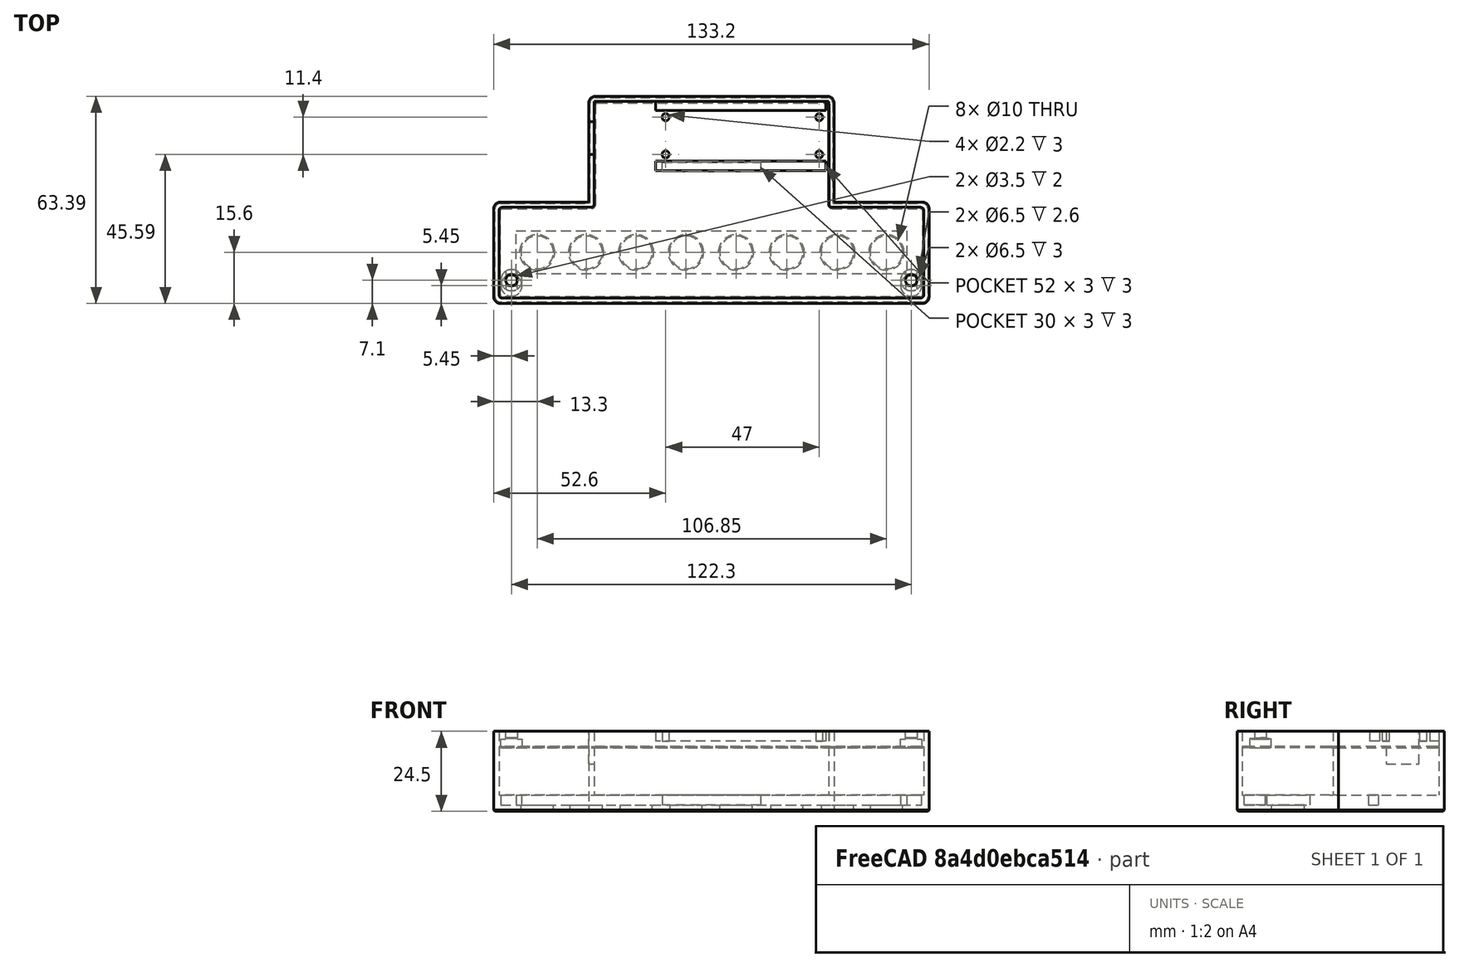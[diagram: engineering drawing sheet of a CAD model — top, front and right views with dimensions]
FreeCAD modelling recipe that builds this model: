
FCSTD DOCUMENT  (FreeCAD 0.21R33771 (Git))
Label: Makerverse_Keyboard_Case_V1
License: All rights reserved
LicenseURL: https://en.wikipedia.org/wiki/All_rights_reserved
objects: TechDraw::DrawViewDimension×38, Sketcher::SketchObject×12, PartDesign::Pocket×10, TechDraw::DrawViewPart×4, PartDesign::Pad×2, PartDesign::Chamfer×2, PartDesign::Body×2, TechDraw::DrawSVGTemplate×1, TechDraw::DrawPage×1
note: 106 computed .brp shape members not serialized (recipe doc carries the construction recipe); baked Part::Feature solids carry a one-line shape summary decoded from their .brp

FEATURE [Sketcher::SketchObject] Sketch
  FullyConstrained = true
  MapMode = 5
  Support = -> [XY_Plane]
  sketch-geometry (20):
    g0: LineSegment StartX=2 StartY=0 StartZ=0 EndX=131.2 EndY=0 EndZ=0
    g1: LineSegment StartX=133.2 StartY=2 StartZ=0 EndX=133.2 EndY=29 EndZ=0
    g2: LineSegment StartX=131.2 StartY=31 StartZ=0 EndX=104.1 EndY=31 EndZ=0
    g3: LineSegment StartX=104.1 StartY=31 StartZ=0 EndX=104.1 EndY=61.39 EndZ=0
    g4: LineSegment StartX=102.1 StartY=63.39 StartZ=0 EndX=31.1 EndY=63.39 EndZ=0
    g5: LineSegment StartX=29.1 StartY=61.39 StartZ=0 EndX=29.1 EndY=31 EndZ=0
    g6: LineSegment StartX=29.1 StartY=31 StartZ=0 EndX=2 EndY=31 EndZ=0
    g7: LineSegment StartX=0 StartY=29 StartZ=0 EndX=0 EndY=2 EndZ=0
    g8: ArcOfCircle CenterX=31.1 CenterY=61.39 CenterZ=0 NormalX=0 NormalY=0 NormalZ=1 AngleXU=0 Radius=2 StartAngle=1.5708 EndAngle=3.14159
    g9: GeomPoint X=29.1 Y=63.39 Z=0
    g10: ArcOfCircle CenterX=102.1 CenterY=61.39 CenterZ=0 NormalX=0 NormalY=0 NormalZ=1 AngleXU=0 Radius=2 StartAngle=-1.8e-15 EndAngle=1.5708
    g11: GeomPoint X=104.1 Y=63.39 Z=0
    g12: ArcOfCircle CenterX=131.2 CenterY=29 CenterZ=0 NormalX=0 NormalY=0 NormalZ=1 AngleXU=0 Radius=2 StartAngle=0 EndAngle=1.5708
    g13: GeomPoint X=133.2 Y=31 Z=0
    g14: ArcOfCircle CenterX=131.2 CenterY=2 CenterZ=0 NormalX=0 NormalY=0 NormalZ=1 AngleXU=0 Radius=2 StartAngle=4.71239 EndAngle=6.28319
    g15: GeomPoint X=133.2 Y=0 Z=0
    g16: ArcOfCircle CenterX=2 CenterY=2 CenterZ=0 NormalX=0 NormalY=0 NormalZ=1 AngleXU=0 Radius=2 StartAngle=3.14159 EndAngle=4.71239
    g17: GeomPoint X=0 Y=0 Z=0
    g18: ArcOfCircle CenterX=2 CenterY=29 CenterZ=0 NormalX=0 NormalY=0 NormalZ=1 AngleXU=0 Radius=2 StartAngle=1.5708 EndAngle=3.14159
    g19: GeomPoint X=0 Y=31 Z=0
  constraints (47):
    c: Coincident(g-1,g17)
    c: PointOnObject(g15,g-1)
    c: Vertical(g1)
    c: Horizontal(g2)
    c: Coincident(g2,g3)
    c: Vertical(g3)
    c: Horizontal(g4)
    c: Vertical(g5)
    c: Coincident(g5,g6)
    c: PointOnObject(g19,g-2)
    c: Horizontal(g6)
    c: DistanceX(g17,g15) = 133.2
    c: DistanceX(g19,g6) = 29.1
    c: DistanceX(g2,g13) = 29.1
    c: DistanceY(g17,g19) = 31
    c: DistanceY(g2,g5) = 0
    c: PointOnObject(g9,g5)
    c: PointOnObject(g9,g4)
    c: Tangent(g5,g8) = -1.5708
    c: Tangent(g4,g8) = -1.5708
    c: DistanceX(g5,g8) = 2
    c: PointOnObject(g11,g3)
    c: PointOnObject(g11,g4)
    c: Tangent(g3,g10) = -1.5708
    c: Tangent(g4,g10) = -1.5708
    c: PointOnObject(g13,g2)
    c: PointOnObject(g13,g1)
    c: Tangent(g2,g12) = -1.5708
    c: Tangent(g1,g12) = -1.5708
    c: PointOnObject(g15,g0)
    c: PointOnObject(g15,g1)
    c: Tangent(g0,g14) = -1.5708
    c: Tangent(g1,g14) = -1.5708
    c: PointOnObject(g17,g0)
    c: PointOnObject(g17,g7)
    c: Tangent(g0,g16) = -1.5708
    c: Tangent(g7,g16) = -1.5708
    c: PointOnObject(g19,g7)
    c: PointOnObject(g19,g6)
    c: Tangent(g7,g18) = -1.5708
    c: Tangent(g6,g18) = -1.5708
    c: DistanceX(g7,g18) = 2
    c: DistanceX(g7,g16) = 2
    c: DistanceX(g12,g1) = 2
    c: DistanceX(g10,g3) = 2
    c: DistanceY(g0,g14) = 2
    c: DistanceY(g5,g8) = 30.39
FEATURE [PartDesign::Pad] Pad
  Direction = (0,0,1)
  Length = 24.5
  Length2 = 10
  Profile = -> Sketch
  ReferenceAxis = -> Sketch [N_Axis]
  Type = 0
FEATURE [Sketcher::SketchObject] Sketch001
  ExternalGeometry = -> [Pad]
  FullyConstrained = true
  MapMode = 5
  Placement = pos=(0,0,0) rot=(1,0,0;3.14159rad)
  Support = -> [Pad]
  sketch-geometry (20):
    g0: LineSegment StartX=2.6 StartY=-1.6 StartZ=0 EndX=130.6 EndY=-1.6 EndZ=0
    g1: LineSegment StartX=131.6 StartY=-2.6 StartZ=0 EndX=131.6 EndY=-28.4 EndZ=0
    g2: LineSegment StartX=130.6 StartY=-29.4 StartZ=0 EndX=103.5 EndY=-29.4 EndZ=0
    g3: LineSegment StartX=102.5 StartY=-30.4 StartZ=0 EndX=102.5 EndY=-61.79 EndZ=0
    g4: LineSegment StartX=102.5 StartY=-61.79 StartZ=0 EndX=30.7 EndY=-61.79 EndZ=0
    g5: LineSegment StartX=30.7 StartY=-61.79 StartZ=0 EndX=30.7 EndY=-30.4 EndZ=0
    g6: LineSegment StartX=29.7 StartY=-29.4 StartZ=0 EndX=2.6 EndY=-29.4 EndZ=0
    g7: LineSegment StartX=1.6 StartY=-28.4 StartZ=0 EndX=1.6 EndY=-2.6 EndZ=0
    g8: ArcOfCircle CenterX=2.6 CenterY=-2.6 CenterZ=0 NormalX=0 NormalY=0 NormalZ=1 AngleXU=0 Radius=1 StartAngle=1.5708 EndAngle=3.14159
    g9: GeomPoint X=1.6 Y=-1.6 Z=0
    g10: ArcOfCircle CenterX=2.6 CenterY=-28.4 CenterZ=0 NormalX=0 NormalY=0 NormalZ=1 AngleXU=0 Radius=1 StartAngle=3.14159 EndAngle=4.71239
    g11: GeomPoint X=1.6 Y=-29.4 Z=0
    g12: ArcOfCircle CenterX=29.7 CenterY=-30.4 CenterZ=0 NormalX=0 NormalY=0 NormalZ=1 AngleXU=0 Radius=1 StartAngle=0 EndAngle=1.5708
    g13: GeomPoint X=30.7 Y=-29.4 Z=0
    g14: ArcOfCircle CenterX=103.5 CenterY=-30.4 CenterZ=0 NormalX=0 NormalY=0 NormalZ=1 AngleXU=0 Radius=1 StartAngle=1.5708 EndAngle=3.14159
    g15: GeomPoint X=102.5 Y=-29.4 Z=0
    g16: ArcOfCircle CenterX=130.6 CenterY=-28.4 CenterZ=0 NormalX=0 NormalY=0 NormalZ=1 AngleXU=0 Radius=1 StartAngle=4.71239 EndAngle=6.28319
    g17: GeomPoint X=131.6 Y=-29.4 Z=0
    g18: ArcOfCircle CenterX=130.6 CenterY=-2.6 CenterZ=0 NormalX=0 NormalY=0 NormalZ=1 AngleXU=0 Radius=1 StartAngle=0 EndAngle=1.5708
    g19: GeomPoint X=131.6 Y=-1.6 Z=0
  constraints (49):
    c: Horizontal(g0)
    c: Vertical(g1)
    c: Horizontal(g2)
    c: Vertical(g3)
    c: Coincident(g3,g4)
    c: Horizontal(g4)
    c: Coincident(g4,g5)
    c: Vertical(g5)
    c: Horizontal(g6)
    c: Parallel(g7,g-2)
    c: DistanceX(g9,g19) = 130
    c: DistanceX(g-1,g-3) = 133.2
    c: DistanceX(g-1,g9) = 1.6
    c: DistanceY(g9,g-1) = 1.6
    c: DistanceY(g-4,g11) = 1.6
    c: DistanceX(g-4,g13) = 1.6
    c: DistanceY(g-6,g17) = 1.6
    c: DistanceX(g15,g-6) = 1.6
    c: DistanceY(g-5,g3) = 1.6
    c: PointOnObject(g9,g7)
    c: PointOnObject(g9,g0)
    c: Tangent(g7,g8) = 1.5708
    c: Tangent(g0,g8) = 1.5708
    c: DistanceX(g7,g8) = 1
    c: PointOnObject(g11,g6)
    c: PointOnObject(g11,g7)
    c: Tangent(g6,g10) = 1.5708
    c: Tangent(g7,g10) = 1.5708
    c: PointOnObject(g13,g5)
    c: PointOnObject(g13,g6)
    c: Tangent(g5,g12) = -1.5708
    c: Tangent(g6,g12) = -1.5708
    c: PointOnObject(g15,g3)
    c: PointOnObject(g15,g2)
    c: Tangent(g3,g14) = -1.5708
    c: Tangent(g2,g14) = -1.5708
    c: PointOnObject(g17,g2)
    c: PointOnObject(g17,g1)
    c: Tangent(g2,g16) = 1.5708
    c: Tangent(g1,g16) = 1.5708
    c: PointOnObject(g19,g1)
    c: PointOnObject(g19,g0)
    c: Tangent(g1,g18) = 1.5708
    c: Tangent(g0,g18) = 1.5708
    c: DistanceX(g18,g1) = 1
    c: DistanceX(g16,g1) = 1
    c: DistanceY(g14,g2) = 1
    c: DistanceX(g12,g5) = 1
    c: DistanceY(g6,g10) = 1
FEATURE [PartDesign::Pocket] Pocket
  BaseFeature = -> Pad
  Direction = (0,0,1)
  Length = 19.5
  Length2 = 5
  Profile = -> Sketch001
  ReferenceAxis = -> Sketch001 [N_Axis]
  Type = 0
FEATURE [Sketcher::SketchObject] Sketch002
  ExternalGeometry = -> [Pocket]
  FullyConstrained = true
  MapMode = 5
  Placement = pos=(0,0,19.5) rot=(1,0,0;3.14159rad)
  Support = -> [Pocket]
  sketch-geometry (4):
    g0: LineSegment StartX=126.4 StartY=-22.2 StartZ=0 EndX=6.8 EndY=-22.2 EndZ=0
    g1: LineSegment StartX=6.8 StartY=-22.2 StartZ=0 EndX=6.8 EndY=-9 EndZ=0
    g2: LineSegment StartX=6.8 StartY=-9 StartZ=0 EndX=126.4 EndY=-9 EndZ=0
    g3: LineSegment StartX=126.4 StartY=-9 StartZ=0 EndX=126.4 EndY=-22.2 EndZ=0
  constraints (12):
    c: Coincident(g0,g1)
    c: Coincident(g1,g2)
    c: Coincident(g2,g3)
    c: Coincident(g3,g0)
    c: Horizontal(g0)
    c: Horizontal(g2)
    c: Vertical(g1)
    c: Vertical(g3)
    c: DistanceY(g3,g3) = 13.2
    c: DistanceX(g0,g-3) = 5.2
    c: DistanceX(g-4,g0) = 5.2
    c: DistanceY(g2,g-5) = 7.4
FEATURE [PartDesign::Pocket] Pocket001
  BaseFeature = -> Pocket
  Direction = (0,0,1)
  Length = 3
  Length2 = 5
  Profile = -> Sketch002
  ReferenceAxis = -> Sketch002 [N_Axis]
  Type = 0
FEATURE [Sketcher::SketchObject] Sketch003
  ExternalGeometry = -> [Pocket001]
  FullyConstrained = true
  MapMode = 5
  Placement = pos=(0,0,22.5) rot=(1,0,0;3.14159rad)
  Support = -> [Pocket001]
  sketch-geometry (9):
    g0: Circle CenterX=59.05 CenterY=-15.6 CenterZ=0 NormalX=0 NormalY=0 NormalZ=1 AngleXU=0 Radius=5
    g1: Circle CenterX=43.55 CenterY=-15.6 CenterZ=0 NormalX=0 NormalY=0 NormalZ=1 AngleXU=0 Radius=5
    g2: Circle CenterX=74.4 CenterY=-15.6 CenterZ=0 NormalX=0 NormalY=0 NormalZ=1 AngleXU=0 Radius=5
    g3: LineSegment StartX=6.8 StartY=-15.6 StartZ=0 EndX=126.4 EndY=-15.6 EndZ=0
    g4: Circle CenterX=28.05 CenterY=-15.6 CenterZ=0 NormalX=0 NormalY=0 NormalZ=1 AngleXU=0 Radius=5
    g5: Circle CenterX=13.05 CenterY=-15.6 CenterZ=0 NormalX=0 NormalY=0 NormalZ=1 AngleXU=0 Radius=5
    g6: Circle CenterX=89.65 CenterY=-15.6 CenterZ=0 NormalX=0 NormalY=0 NormalZ=1 AngleXU=0 Radius=5
    g7: Circle CenterX=104.9 CenterY=-15.6 CenterZ=0 NormalX=0 NormalY=0 NormalZ=1 AngleXU=0 Radius=5
    g8: Circle CenterX=119.9 CenterY=-15.6 CenterZ=0 NormalX=0 NormalY=0 NormalZ=1 AngleXU=0 Radius=5
  constraints (29):
    c: Diameter(g0) = 10
    c: DistanceX(g1,g0) = 15.5
    c: Diameter(g2) = 10
    c: Diameter(g1) = 10
    c: PointOnObject(g3,g-3)
    c: PointOnObject(g3,g-4)
    c: Horizontal(g3)
    c: DistanceY(g3,g-4) = 6.6
    c: PointOnObject(g2,g3)
    c: PointOnObject(g1,g3)
    c: PointOnObject(g0,g3)
    c: PointOnObject(g4,g3)
    c: PointOnObject(g5,g3)
    c: Diameter(g4) = 10
    c: Diameter(g5) = 10
    c: DistanceX(g4,g1) = 15.5
    c: DistanceX(g5,g4) = 15
    c: PointOnObject(g6,g3)
    c: PointOnObject(g7,g3)
    c: PointOnObject(g8,g3)
    c: DistanceX(g7,g8) = 15
    c: Diameter(g6) = 10
    c: Diameter(g7) = 10
    c: Diameter(g8) = 10
    c: DistanceX(g3,g5) = 6.25
    c: DistanceX(g8,g-4) = 6.5
    c: DistanceX(g6,g7) = 15.25
    c: DistanceX(g2,g6) = 15.25
    c: DistanceY(g-4,g-4) = 13.2
FEATURE [PartDesign::Pocket] Pocket002
  BaseFeature = -> Pocket001
  Direction = (0,0,1)
  Length = 5
  Length2 = 5
  Profile = -> Sketch003
  ReferenceAxis = -> Sketch003 [N_Axis]
  Type = 1
FEATURE [Sketcher::SketchObject] Sketch006
  FullyConstrained = true
  MapMode = 5
  Support = -> [XY_Plane001]
  sketch-geometry (24):
    g0: LineSegment StartX=2.6 StartY=29.4 StartZ=0 EndX=29.6 EndY=29.4 EndZ=0
    g1: LineSegment StartX=30.6 StartY=30.4 StartZ=0 EndX=30.6 EndY=60.79 EndZ=0
    g2: LineSegment StartX=31.6 StartY=61.79 StartZ=0 EndX=101.4 EndY=61.79 EndZ=0
    g3: LineSegment StartX=102.4 StartY=60.79 StartZ=0 EndX=102.4 EndY=30.4 EndZ=0
    g4: LineSegment StartX=103.4 StartY=29.4 StartZ=0 EndX=130.6 EndY=29.4 EndZ=0
    g5: LineSegment StartX=131.6 StartY=28.4 StartZ=0 EndX=131.6 EndY=2.6 EndZ=0
    g6: LineSegment StartX=130.6 StartY=1.6 StartZ=0 EndX=2.6 EndY=1.6 EndZ=0
    g7: LineSegment StartX=1.6 StartY=28.4 StartZ=0 EndX=1.6 EndY=2.6 EndZ=0
    g8: ArcOfCircle CenterX=2.6 CenterY=2.6 CenterZ=0 NormalX=0 NormalY=0 NormalZ=1 AngleXU=0 Radius=1 StartAngle=3.14159 EndAngle=4.71239
    g9: GeomPoint X=1.6 Y=1.6 Z=0
    g10: ArcOfCircle CenterX=130.6 CenterY=2.6 CenterZ=0 NormalX=0 NormalY=0 NormalZ=1 AngleXU=0 Radius=1 StartAngle=4.71239 EndAngle=6.28319
    g11: GeomPoint X=131.6 Y=1.6 Z=0
    g12: ArcOfCircle CenterX=130.6 CenterY=28.4 CenterZ=0 NormalX=0 NormalY=0 NormalZ=1 AngleXU=0 Radius=1 StartAngle=1.1e-15 EndAngle=1.5708
    g13: GeomPoint X=131.6 Y=29.4 Z=0
    g14: ArcOfCircle CenterX=2.6 CenterY=28.4 CenterZ=0 NormalX=0 NormalY=0 NormalZ=1 AngleXU=0 Radius=1 StartAngle=1.5708 EndAngle=3.14159
    g15: GeomPoint X=1.6 Y=29.4 Z=0
    g16: ArcOfCircle CenterX=31.6 CenterY=60.79 CenterZ=0 NormalX=0 NormalY=0 NormalZ=1 AngleXU=0 Radius=1 StartAngle=1.5708 EndAngle=3.14159
    g17: GeomPoint X=30.6 Y=61.79 Z=0
    g18: ArcOfCircle CenterX=29.6 CenterY=30.4 CenterZ=0 NormalX=0 NormalY=0 NormalZ=1 AngleXU=0 Radius=1 StartAngle=4.71239 EndAngle=6.28319
    g19: GeomPoint X=30.6 Y=29.4 Z=0
    g20: ArcOfCircle CenterX=103.4 CenterY=30.4 CenterZ=0 NormalX=0 NormalY=0 NormalZ=1 AngleXU=0 Radius=1 StartAngle=3.14159 EndAngle=4.71239
    g21: GeomPoint X=102.4 Y=29.4 Z=0
    g22: ArcOfCircle CenterX=101.4 CenterY=60.79 CenterZ=0 NormalX=0 NormalY=0 NormalZ=1 AngleXU=0 Radius=1 StartAngle=-1.8e-15 EndAngle=1.5708
    g23: GeomPoint X=102.4 Y=61.79 Z=0
  constraints (56):
    c: Horizontal(g0)
    c: Vertical(g1)
    c: Horizontal(g2)
    c: Vertical(g3)
    c: Horizontal(g4)
    c: Vertical(g5)
    c: Horizontal(g6)
    c: Vertical(g7)
    c: DistanceX(g9,g11) = 130
    c: DistanceY(g11,g13) = 27.8
    c: DistanceY(g19,g21) = 0
    c: DistanceX(g21,g13) = 29.2
    c: DistanceX(g17,g23) = 71.8
    c: DistanceY(g21,g23) = 32.39
    c: DistanceX(g-1,g9) = 1.6
    c: DistanceY(g-1,g9) = 1.6
    c: PointOnObject(g9,g6)
    c: PointOnObject(g9,g7)
    c: Tangent(g6,g8) = 1.5708
    c: Tangent(g7,g8) = -1.5708
    c: PointOnObject(g11,g6)
    c: PointOnObject(g11,g5)
    c: Tangent(g6,g10) = 1.5708
    c: Tangent(g5,g10) = 1.5708
    c: PointOnObject(g13,g5)
    c: PointOnObject(g13,g4)
    c: Tangent(g5,g12) = 1.5708
    c: Tangent(g4,g12) = 1.5708
    c: PointOnObject(g15,g7)
    c: PointOnObject(g15,g0)
    c: Tangent(g7,g14) = -1.5708
    c: Tangent(g0,g14) = 1.5708
    c: DistanceX(g7,g14) = 1
    c: DistanceX(g7,g8) = 1
    c: DistanceX(g10,g5) = 1
    c: DistanceX(g12,g5) = 1
    c: PointOnObject(g17,g1)
    c: PointOnObject(g17,g2)
    c: Tangent(g1,g16) = 1.5708
    c: Tangent(g2,g16) = 1.5708
    c: PointOnObject(g19,g0)
    c: PointOnObject(g19,g1)
    c: Tangent(g0,g18) = -1.5708
    c: Tangent(g1,g18) = -1.5708
    c: PointOnObject(g21,g4)
    c: PointOnObject(g21,g3)
    c: Tangent(g4,g20) = -1.5708
    c: Tangent(g3,g20) = -1.5708
    c: PointOnObject(g23,g3)
    c: PointOnObject(g23,g2)
    c: Tangent(g3,g22) = 1.5708
    c: Tangent(g2,g22) = 1.5708
    c: DistanceX(g1,g16) = 1
    c: DistanceX(g18,g1) = 1
    c: DistanceX(g3,g20) = 1
    c: DistanceX(g22,g3) = 1
FEATURE [PartDesign::Pad] Pad001
  Direction = (0,0,1)
  Length = 5
  Length2 = 10
  Profile = -> Sketch006
  ReferenceAxis = -> Sketch006 [N_Axis]
  Type = 0
FEATURE [Sketcher::SketchObject] Sketch007
  ExternalGeometry = -> [Pocket002]
  FullyConstrained = true
  MapMode = 5
  Placement = pos=(0,0,19.5) rot=(1,0,0;3.14159rad)
  Support = -> [Pocket002]
  sketch-geometry (6):
    g0: LineSegment StartX=51.6 StartY=-40.2 StartZ=0 EndX=81.6 EndY=-40.2 EndZ=0
    g1: LineSegment StartX=81.6 StartY=-40.2 StartZ=0 EndX=81.6 EndY=-43.2 EndZ=0
    g2: LineSegment StartX=81.6 StartY=-43.2 StartZ=0 EndX=51.6 EndY=-43.2 EndZ=0
    g3: LineSegment StartX=51.6 StartY=-43.2 StartZ=0 EndX=51.6 EndY=-40.2 EndZ=0
    g4: Circle CenterX=5.45 CenterY=-5.45 CenterZ=0 NormalX=0 NormalY=0 NormalZ=1 AngleXU=0 Radius=3.25
    g5: Circle CenterX=127.75 CenterY=-5.45 CenterZ=0 NormalX=0 NormalY=0 NormalZ=1 AngleXU=0 Radius=3.25
  constraints (19):
    c: Coincident(g0,g1)
    c: Coincident(g1,g2)
    c: Coincident(g2,g3)
    c: Coincident(g3,g0)
    c: Horizontal(g0)
    c: Horizontal(g2)
    c: Vertical(g1)
    c: Vertical(g3)
    c: DistanceY(g3,g3) = 3
    c: DistanceX(g0,g0) = 30
    c: Diameter(g4) = 6.5
    c: Diameter(g5) = 6.5
    c: DistanceY(g4,g-4) = 3.85
    c: DistanceX(g-3,g4) = 3.85
    c: DistanceY(g5,g-4) = 3.85
    c: DistanceX(g5,g-4) = 2.85
    c: DistanceY(g0,g-5) = 18
    c: DistanceX(g-6,g-7) = 71.8
    c: DistanceX(g0,g-7) = 20.9
FEATURE [PartDesign::Pocket] Pocket003
  BaseFeature = -> Pocket002
  Direction = (0,0,1)
  Length = 3
  Length2 = 5
  Profile = -> Sketch007
  ReferenceAxis = -> Sketch007 [N_Axis]
  Type = 0
FEATURE [Sketcher::SketchObject] Sketch008
  ExternalGeometry = -> [Pocket003]
  FullyConstrained = true
  MapMode = 5
  Placement = pos=(104.1,0,0) rot=(0.57735,0.57735,0.57735;2.0944rad)
  Support = -> [Pocket003]
  sketch-geometry (4):
    g0: LineSegment StartX=45.59 StartY=10 StartZ=0 EndX=55.59 EndY=10 EndZ=0
    g1: LineSegment StartX=55.59 StartY=10 StartZ=0 EndX=55.59 EndY=0 EndZ=0
    g2: LineSegment StartX=55.59 StartY=0 StartZ=0 EndX=45.59 EndY=0 EndZ=0
    g3: LineSegment StartX=45.59 StartY=0 StartZ=0 EndX=45.59 EndY=10 EndZ=0
  constraints (12):
    c: Coincident(g0,g1)
    c: Coincident(g1,g2)
    c: Coincident(g2,g3)
    c: Coincident(g3,g0)
    c: Horizontal(g0)
    c: Horizontal(g2)
    c: Vertical(g1)
    c: Vertical(g3)
    c: PointOnObject(g1,g-1)
    c: DistanceX(g2,g2) = 10
    c: DistanceX(g-4,g0) = 5.39
    c: DistanceY(g1,g1) = 10
FEATURE [PartDesign::Pocket] Pocket004
  BaseFeature = -> Pocket003
  Direction = (-1,0,0)
  Length = 5
  Length2 = 5
  Profile = -> Sketch008
  ReferenceAxis = -> Sketch008 [N_Axis]
  Type = 0
FEATURE [Sketcher::SketchObject] Sketch009
  ExternalGeometry = -> [Pad001]
  FullyConstrained = true
  MapMode = 5
  Placement = pos=(0,0,0) rot=(1,0,0;3.14159rad)
  Support = -> [Pad001]
  sketch-geometry (12):
    g0: Circle CenterX=33.6 CenterY=-45.59 CenterZ=0 NormalX=0 NormalY=0 NormalZ=1 AngleXU=0 Radius=1.1
    g1: Circle CenterX=33.6 CenterY=-56.99 CenterZ=0 NormalX=0 NormalY=0 NormalZ=1 AngleXU=0 Radius=1.1
    g2: Circle CenterX=80.6 CenterY=-45.59 CenterZ=0 NormalX=0 NormalY=0 NormalZ=1 AngleXU=0 Radius=1.1
    g3: Circle CenterX=80.6 CenterY=-56.99 CenterZ=0 NormalX=0 NormalY=0 NormalZ=1 AngleXU=0 Radius=1.1
    g4: LineSegment StartX=31.6 StartY=-58.99 StartZ=0 EndX=83.6 EndY=-58.99 EndZ=0
    g5: LineSegment StartX=83.6 StartY=-58.99 StartZ=0 EndX=83.6 EndY=-61.79 EndZ=0
    g6: LineSegment StartX=83.6 StartY=-61.79 StartZ=0 EndX=31.6 EndY=-61.79 EndZ=0
    g7: LineSegment StartX=31.6 StartY=-61.79 StartZ=0 EndX=31.6 EndY=-58.99 EndZ=0
    g8: LineSegment StartX=31.6 StartY=-40.59 StartZ=0 EndX=83.6 EndY=-40.59 EndZ=0
    g9: LineSegment StartX=83.6 StartY=-40.59 StartZ=0 EndX=83.6 EndY=-43.59 EndZ=0
    g10: LineSegment StartX=83.6 StartY=-43.59 StartZ=0 EndX=31.6 EndY=-43.59 EndZ=0
    g11: LineSegment StartX=31.6 StartY=-43.59 StartZ=0 EndX=31.6 EndY=-40.59 EndZ=0
  constraints (36):
    c: DistanceY(g-4,g1) = 4.8
    c: Diameter(g1) = 2.2
    c: Diameter(g3) = 2.2
    c: Diameter(g2) = 2.2
    c: Diameter(g0) = 2.2
    c: DistanceY(g1,g0) = 11.4
    c: DistanceY(g3,g2) = 11.4
    c: DistanceX(g-3,g1) = 3
    c: DistanceX(g1,g0) = 0
    c: DistanceX(g0,g2) = 47
    c: DistanceX(g3,g2) = 0
    c: DistanceY(g0,g2) = 0
    c: Coincident(g4,g5)
    c: Coincident(g5,g6)
    c: Coincident(g6,g7)
    c: Coincident(g7,g4)
    c: Horizontal(g4)
    c: Horizontal(g6)
    c: Vertical(g5)
    c: Vertical(g7)
    c: Coincident(g8,g9)
    c: Coincident(g9,g10)
    c: Coincident(g10,g11)
    c: Coincident(g11,g8)
    c: Horizontal(g8)
    c: Horizontal(g10)
    c: Vertical(g9)
    c: Vertical(g11)
    c: DistanceX(g10,g10) = 52
    c: DistanceX(g10,g0) = 2
    c: DistanceY(g0,g10) = 2
    c: DistanceY(g11,g11) = 3
    c: DistanceY(g4,g1) = 2
    c: DistanceX(g4,g1) = 2
    c: DistanceX(g4,g4) = 52
    c: DistanceY(g-4,g6) = 0
FEATURE [PartDesign::Pocket] Pocket005
  BaseFeature = -> Pad001
  Direction = (0,0,1)
  Length = 3
  Length2 = 5
  Profile = -> Sketch009
  ReferenceAxis = -> Sketch009 [N_Axis]
  Type = 0
FEATURE [Sketcher::SketchObject] Sketch010
  ExternalGeometry = -> [Pocket005]
  FullyConstrained = true
  MapMode = 5
  Placement = pos=(0,0,5) rot=(0,0,1;0rad)
  Support = -> [Pocket005]
  sketch-geometry (2):
    g0: Circle CenterX=5.45 CenterY=7.1 CenterZ=0 NormalX=0 NormalY=0 NormalZ=1 AngleXU=0 Radius=1.75
    g1: Circle CenterX=127.75 CenterY=7.1 CenterZ=0 NormalX=0 NormalY=0 NormalZ=1 AngleXU=0 Radius=1.75
  constraints (6):
    c: Diameter(g0) = 3.5
    c: Diameter(g1) = 3.5
    c: DistanceX(g-4,g0) = 3.85
    c: DistanceY(g-6,g0) = 5.5
    c: DistanceY(g-6,g1) = 5.5
    c: DistanceX(g1,g-3) = 3.85
FEATURE [PartDesign::Pocket] Pocket006
  BaseFeature = -> Pocket005
  Direction = (0,0,-1)
  Length = 5
  Length2 = 5
  Profile = -> Sketch010
  ReferenceAxis = -> Sketch010 [N_Axis]
  Type = 1
FEATURE [Sketcher::SketchObject] Sketch011
  ExternalGeometry = -> [Pocket006]
  FullyConstrained = true
  MapMode = 5
  Placement = pos=(0,0,5) rot=(0,0,1;0rad)
  Support = -> [Pocket006]
  sketch-geometry (2):
    g0: Circle CenterX=5.45 CenterY=7.1 CenterZ=0 NormalX=0 NormalY=0 NormalZ=1 AngleXU=0 Radius=3.25
    g1: Circle CenterX=127.75 CenterY=7.1 CenterZ=0 NormalX=0 NormalY=0 NormalZ=1 AngleXU=0 Radius=3.25
  constraints (4):
    c: Diameter(g1) = 6.5
    c: Diameter(g0) = 6.5
    c: Coincident(g0,g-4)
    c: Coincident(g-3,g1)
FEATURE [PartDesign::Pocket] Pocket007
  BaseFeature = -> Pocket006
  Direction = (0,0,-1)
  Length = 2.6
  Length2 = 5
  Profile = -> Sketch011
  ReferenceAxis = -> Sketch011 [N_Axis]
  Type = 0
FEATURE [Sketcher::SketchObject] Sketch012
  ExternalGeometry = -> [Pocket007]
  FullyConstrained = true
  MapMode = 5
  Placement = pos=(0,0,2.4) rot=(0,0,1;0rad)
  Support = -> [Pocket007]
  sketch-geometry (8):
    g0: LineSegment StartX=3.7 StartY=4.36139 StartZ=0 EndX=3.7 EndY=9.83861 EndZ=0
    g1: LineSegment StartX=7.2 StartY=9.83861 StartZ=0 EndX=7.2 EndY=4.36139 EndZ=0
    g2: LineSegment StartX=126 StartY=4.36139 StartZ=0 EndX=126 EndY=9.83861 EndZ=0
    g3: LineSegment StartX=129.5 StartY=9.83861 StartZ=0 EndX=129.5 EndY=4.36139 EndZ=0
    g4: ArcOfCircle CenterX=127.75 CenterY=7.1 CenterZ=0 NormalX=0 NormalY=0 NormalZ=1 AngleXU=0 Radius=3.25 StartAngle=4.14378 EndAngle=5.281
    g5: ArcOfCircle CenterX=127.75 CenterY=7.1 CenterZ=0 NormalX=0 NormalY=0 NormalZ=1 AngleXU=0 Radius=3.25 StartAngle=1.00219 EndAngle=2.13941
    g6: ArcOfCircle CenterX=5.45 CenterY=7.1 CenterZ=0 NormalX=0 NormalY=0 NormalZ=1 AngleXU=0 Radius=3.25 StartAngle=1.00219 EndAngle=2.13941
    g7: ArcOfCircle CenterX=5.45 CenterY=7.1 CenterZ=0 NormalX=0 NormalY=0 NormalZ=1 AngleXU=0 Radius=3.25 StartAngle=4.14378 EndAngle=5.281
  constraints (28):
    c: PointOnObject(g0,g-5)
    c: Vertical(g0)
    c: PointOnObject(g1,g-5)
    c: PointOnObject(g1,g-5)
    c: Vertical(g1)
    c: PointOnObject(g2,g-8)
    c: PointOnObject(g2,g-8)
    c: Vertical(g2)
    c: PointOnObject(g3,g-8)
    c: PointOnObject(g3,g-8)
    c: Vertical(g3)
    c: Tangent(g3,g-7)
    c: Tangent(g2,g-7)
    c: Tangent(g0,g-6)
    c: Tangent(g1,g-6)
    c: PointOnObject(g0,g-5)
    c: Coincident(g4,g3)
    c: Coincident(g4,g2)
    c: Tangent(g4,g-8)
    c: Coincident(g5,g2)
    c: Coincident(g5,g3)
    c: Tangent(g5,g-8)
    c: Coincident(g6,g0)
    c: Coincident(g6,g1)
    c: Tangent(g6,g-5)
    c: Coincident(g7,g0)
    c: Coincident(g7,g1)
    c: Tangent(g7,g-5)
FEATURE [PartDesign::Pocket] Pocket008
  BaseFeature = -> Pocket007
  Direction = (0,0,-1)
  Length = 0.2
  Length2 = 5
  Profile = -> Sketch012
  ReferenceAxis = -> Sketch012 [N_Axis]
  Type = 0
FEATURE [Sketcher::SketchObject] Sketch013
  ExternalGeometry = -> [Pocket008]
  FullyConstrained = true
  MapMode = 5
  Placement = pos=(0,0,2.2) rot=(0,0,1;0rad)
  Support = -> [Pocket008]
  sketch-geometry (8):
    g0: LineSegment StartX=3.7 StartY=8.85 StartZ=0 EndX=7.2 EndY=8.85 EndZ=0
    g1: LineSegment StartX=7.2 StartY=8.85 StartZ=0 EndX=7.2 EndY=5.35 EndZ=0
    g2: LineSegment StartX=7.2 StartY=5.35 StartZ=0 EndX=3.7 EndY=5.35 EndZ=0
    g3: LineSegment StartX=3.7 StartY=5.35 StartZ=0 EndX=3.7 EndY=8.85 EndZ=0
    g4: LineSegment StartX=126 StartY=8.85 StartZ=0 EndX=129.5 EndY=8.85 EndZ=0
    g5: LineSegment StartX=129.5 StartY=8.85 StartZ=0 EndX=129.5 EndY=5.35 EndZ=0
    g6: LineSegment StartX=129.5 StartY=5.35 StartZ=0 EndX=126 EndY=5.35 EndZ=0
    g7: LineSegment StartX=126 StartY=5.35 StartZ=0 EndX=126 EndY=8.85 EndZ=0
  constraints (24):
    c: Coincident(g0,g1)
    c: Coincident(g1,g2)
    c: Coincident(g2,g3)
    c: Coincident(g3,g0)
    c: Horizontal(g0)
    c: Horizontal(g2)
    c: Vertical(g1)
    c: Vertical(g3)
    c: PointOnObject(g0,g-8)
    c: PointOnObject(g1,g-7)
    c: Coincident(g4,g5)
    c: Coincident(g5,g6)
    c: Coincident(g6,g7)
    c: Coincident(g7,g4)
    c: Horizontal(g4)
    c: Horizontal(g6)
    c: Vertical(g5)
    c: Vertical(g7)
    c: PointOnObject(g4,g-9)
    c: PointOnObject(g5,g-10)
    c: Tangent(g6,g-11)
    c: Tangent(g4,g-12)
    c: Tangent(g2,g-13)
    c: Tangent(g0,g-6)
FEATURE [PartDesign::Pocket] Pocket009
  BaseFeature = -> Pocket008
  Direction = (0,0,-1)
  Length = 0.2
  Length2 = 5
  Profile = -> Sketch013
  ReferenceAxis = -> Sketch013 [N_Axis]
  Type = 0
FEATURE [PartDesign::Chamfer] Chamfer
  Angle = 45
  Base = -> Pocket004 [Face5]
  BaseFeature = -> Pocket004
  ChamferType = 0
  FlipDirection = false
  Size = 0.4
  Size2 = 1
  SupportTransform = false
  UseAllEdges = false
FEATURE [PartDesign::Body] Body  label="Cover"
  Group = -> [Sketch,Pad,Sketch001,Pocket,Sketch002,Pocket001,Sketch003,Pocket002,Sketch007,Pocket003,Sketch008,Pocket004,Chamfer]
  Origin = -> Origin
  Placement = pos=(0,0,0) rot=(0,1,0;3.14159rad)
  Tip = -> Chamfer
FEATURE [PartDesign::Chamfer] Chamfer001
  Angle = 45
  Base = -> Pocket009 [Edge10]
  BaseFeature = -> Pocket009
  ChamferType = 0
  FlipDirection = false
  Size = 0.4
  Size2 = 1
  SupportTransform = false
  UseAllEdges = false
FEATURE [PartDesign::Body] Body001  label="Base"
  Group = -> [Sketch006,Pad001,Sketch009,Pocket005,Sketch010,Pocket006,Sketch011,Pocket007,Sketch012,Pocket008,Sketch013,Pocket009,Chamfer001]
  Origin = -> Origin001
  Placement = pos=(0,0,0) rot=(0,1,0;3.14159rad)
  Tip = -> Chamfer001
FEATURE [TechDraw::DrawSVGTemplate] Template
  EditableTexts = Designed_by_Name=Dan; Drawing_number=1; FC-Date=05/08/2024; FC-SC=0.75; FC-SH=1 of 1; FC-Title=Makerverse Keyboard Case; Weight=0.054
  Height = 210
  Orientation = 1
  Template = <userpath>/AppData/Local/Programs/FreeCAD 0.21/data/Mod/TechDraw/Templates/A4_LandscapeTD.svg
  Width = 297
FEATURE [TechDraw::DrawViewPart] View002  label="Cover TopDown"
  CoarseView = false
  Direction = (0,0,1)
  Focus = 100
  HardHidden = false
  IsoCount = 0
  IsoHidden = false
  IsoVisible = false
  LockPosition = false
  Perspective = false
  Rotation = 0
  Scale = 0.75
  ScaleType = 0
  ScrubCount = 0
  SeamHidden = false
  SeamVisible = false
  SmoothHidden = false
  SmoothVisible = true
  Source = -> [Body]
  X = 47.9217
  XDirection = (1e-06,-1,0)
  Y = 114.013
FEATURE [TechDraw::DrawViewDimension] Dimension
  AngleOverride = false
  Arbitrary = false
  ArbitraryTolerances = false
  EqualTolerance = true
  ExtensionAngle = 0
  FormatSpec = ⌀%.2w
  FormatSpecOverTolerance = %+.2w
  FormatSpecUnderTolerance = %+.2w
  Inverted = false
  LineAngle = 0
  LockPosition = false
  MeasureType = 1
  OverTolerance = 0
  References2D = -> [View002]
  Rotation = 0
  Scale = 0.75
  ScaleType = 0
  TheoreticalExact = false
  Type = 5
  UnderTolerance = 0
  X = -16.1256
  Y = 49.3846
FEATURE [TechDraw::DrawViewDimension] Dimension001
  AngleOverride = false
  Arbitrary = false
  ArbitraryTolerances = false
  EqualTolerance = true
  ExtensionAngle = 0
  FormatSpec = R%.2w
  FormatSpecOverTolerance = %+.2w
  FormatSpecUnderTolerance = %+.2w
  Inverted = false
  LineAngle = 0
  LockPosition = false
  MeasureType = 1
  OverTolerance = 0
  References2D = -> [View002]
  Rotation = 0
  Scale = 0.75
  ScaleType = 0
  TheoreticalExact = false
  Type = 4
  UnderTolerance = 0
  X = 32.0832
  Y = 58.6232
FEATURE [TechDraw::DrawViewDimension] Dimension002
  AngleOverride = false
  Arbitrary = false
  ArbitraryTolerances = false
  EqualTolerance = true
  ExtensionAngle = 0
  FormatSpec = %.2w
  FormatSpecOverTolerance = %+.2w
  FormatSpecUnderTolerance = %+.2w
  Inverted = false
  LineAngle = 0
  LockPosition = false
  MeasureType = 1
  OverTolerance = 0
  References2D = -> [View002]
  Rotation = 0
  Scale = 0.75
  ScaleType = 0
  TheoreticalExact = false
  Type = 2
  UnderTolerance = 0
  X = 38.8169
  Y = 2.66797
FEATURE [TechDraw::DrawViewDimension] Dimension003
  AngleOverride = false
  Arbitrary = false
  ArbitraryTolerances = false
  EqualTolerance = true
  ExtensionAngle = 0
  FormatSpec = %.2w
  FormatSpecOverTolerance = %+.2w
  FormatSpecUnderTolerance = %+.2w
  Inverted = false
  LineAngle = 0
  LockPosition = false
  MeasureType = 1
  OverTolerance = 0
  References2D = -> [View002]
  Rotation = 0
  Scale = 0.75
  ScaleType = 0
  TheoreticalExact = false
  Type = 1
  UnderTolerance = 0
  X = 12.2041
  Y = 66.8015
FEATURE [TechDraw::DrawViewDimension] Dimension004
  AngleOverride = false
  Arbitrary = false
  ArbitraryTolerances = false
  EqualTolerance = true
  ExtensionAngle = 0
  FormatSpec = %.2w
  FormatSpecOverTolerance = %+.2w
  FormatSpecUnderTolerance = %+.2w
  Inverted = false
  LineAngle = 0
  LockPosition = false
  MeasureType = 1
  OverTolerance = 0
  References2D = -> [View002]
  Rotation = 0
  Scale = 0.75
  ScaleType = 0
  TheoreticalExact = false
  Type = 1
  UnderTolerance = 0
  X = 11.9672
  Y = 83.5957
FEATURE [TechDraw::DrawViewDimension] Dimension005
  AngleOverride = false
  Arbitrary = false
  ArbitraryTolerances = false
  EqualTolerance = true
  ExtensionAngle = 0
  FormatSpec = %.2w
  FormatSpecOverTolerance = %+.2w
  FormatSpecUnderTolerance = %+.2w
  Inverted = false
  LineAngle = 0
  LockPosition = false
  MeasureType = 1
  OverTolerance = 0
  References2D = -> [View002]
  Rotation = 0
  Scale = 0.75
  ScaleType = 0
  TheoreticalExact = false
  Type = 1
  UnderTolerance = 0
  X = 11.9843
  Y = 74.8998
FEATURE [TechDraw::DrawViewDimension] Dimension006
  AngleOverride = false
  Arbitrary = false
  ArbitraryTolerances = false
  EqualTolerance = true
  ExtensionAngle = 0
  FormatSpec = %.2w
  FormatSpecOverTolerance = %+.2w
  FormatSpecUnderTolerance = %+.2w
  Inverted = false
  LineAngle = 0
  LockPosition = false
  MeasureType = 1
  OverTolerance = 0
  References2D = -> [View002]
  Rotation = 0
  Scale = 0.75
  ScaleType = 0
  TheoreticalExact = false
  Type = 1
  UnderTolerance = 0
  X = -9.56734
  Y = 39.8209
FEATURE [TechDraw::DrawViewDimension] Dimension008
  AngleOverride = false
  Arbitrary = false
  ArbitraryTolerances = false
  EqualTolerance = true
  ExtensionAngle = 0
  FormatSpec = %.2w
  FormatSpecOverTolerance = %+.2w
  FormatSpecUnderTolerance = %+.2w
  Inverted = false
  LineAngle = 0
  LockPosition = false
  MeasureType = 1
  OverTolerance = 0
  References2D = -> [View002]
  Rotation = 0
  Scale = 0.75
  ScaleType = 0
  TheoreticalExact = false
  Type = 1
  UnderTolerance = 0
  X = -0.136964
  Y = -75.1684
FEATURE [TechDraw::DrawViewDimension] Dimension009
  AngleOverride = false
  Arbitrary = false
  ArbitraryTolerances = false
  EqualTolerance = true
  ExtensionAngle = 0
  FormatSpec = %.2w
  FormatSpecOverTolerance = %+.2w
  FormatSpecUnderTolerance = %+.2w
  Inverted = false
  LineAngle = 0
  LockPosition = false
  MeasureType = 1
  OverTolerance = 0
  References2D = -> [View002]
  Rotation = 0
  Scale = 0.75
  ScaleType = 0
  TheoreticalExact = false
  Type = 1
  UnderTolerance = 0
  X = -15.4538
  Y = -41.0122
FEATURE [TechDraw::DrawViewDimension] Dimension010
  AngleOverride = false
  Arbitrary = false
  ArbitraryTolerances = false
  EqualTolerance = true
  ExtensionAngle = 0
  FormatSpec = %.2w
  FormatSpecOverTolerance = %+.2w
  FormatSpecUnderTolerance = %+.2w
  Inverted = false
  LineAngle = 0
  LockPosition = false
  MeasureType = 1
  OverTolerance = 0
  References2D = -> [View002]
  Rotation = 0
  Scale = 0.75
  ScaleType = 0
  TheoreticalExact = false
  Type = 1
  UnderTolerance = 0
  X = -33.1444
  Y = -18.5532
FEATURE [TechDraw::DrawViewDimension] Dimension011
  AngleOverride = false
  Arbitrary = false
  ArbitraryTolerances = false
  EqualTolerance = true
  ExtensionAngle = 0
  FormatSpec = %.2w
  FormatSpecOverTolerance = %+.2w
  FormatSpecUnderTolerance = %+.2w
  Inverted = false
  LineAngle = 0
  LockPosition = false
  MeasureType = 1
  OverTolerance = 0
  References2D = -> [View002]
  Rotation = 0
  Scale = 0.75
  ScaleType = 0
  TheoreticalExact = false
  Type = 1
  UnderTolerance = 0
  X = -0.425056
  Y = 25.8775
FEATURE [TechDraw::DrawViewDimension] Dimension012
  AngleOverride = false
  Arbitrary = false
  ArbitraryTolerances = false
  EqualTolerance = true
  ExtensionAngle = 0
  FormatSpec = %.2w
  FormatSpecOverTolerance = %+.2w
  FormatSpecUnderTolerance = %+.2w
  Inverted = false
  LineAngle = 0
  LockPosition = false
  MeasureType = 1
  OverTolerance = 0
  References2D = -> [View002]
  Rotation = 0
  Scale = 0.75
  ScaleType = 0
  TheoreticalExact = false
  Type = 1
  UnderTolerance = 0
  X = -15.7454
  Y = -8.79622
FEATURE [TechDraw::DrawViewDimension] Dimension013
  AngleOverride = false
  Arbitrary = false
  ArbitraryTolerances = false
  EqualTolerance = true
  ExtensionAngle = 0
  FormatSpec = %.2w
  FormatSpecOverTolerance = %+.2w
  FormatSpecUnderTolerance = %+.2w
  Inverted = false
  LineAngle = 0
  LockPosition = false
  MeasureType = 1
  OverTolerance = 0
  References2D = -> [View002]
  Rotation = 0
  Scale = 0.75
  ScaleType = 0
  TheoreticalExact = false
  Type = 1
  UnderTolerance = 0
  X = 33.9449
  Y = -49.3139
FEATURE [TechDraw::DrawViewDimension] Dimension014
  AngleOverride = false
  Arbitrary = false
  ArbitraryTolerances = false
  EqualTolerance = true
  ExtensionAngle = 0
  FormatSpec = ⌀%.2w
  FormatSpecOverTolerance = %+.2w
  FormatSpecUnderTolerance = %+.2w
  Inverted = false
  LineAngle = 0
  LockPosition = false
  MeasureType = 1
  OverTolerance = 0
  References2D = -> [View002]
  Rotation = 0
  Scale = 0.75
  ScaleType = 0
  TheoreticalExact = false
  Type = 5
  UnderTolerance = 0
  X = 52.0717
  Y = -41.9571
FEATURE [TechDraw::DrawViewPart] View  label="Cover Side on"
  CoarseView = false
  Direction = (-1,-1e-06,0)
  Focus = 100
  HardHidden = false
  IsoCount = 0
  IsoHidden = false
  IsoVisible = false
  LockPosition = false
  Perspective = false
  Rotation = 0
  Scale = 0.75
  ScaleType = 0
  ScrubCount = 0
  SeamHidden = false
  SeamVisible = false
  SmoothHidden = false
  SmoothVisible = true
  Source = -> [Body]
  X = 133.186
  XDirection = (1e-06,-1,0)
  Y = 166.598
FEATURE [TechDraw::DrawViewDimension] Dimension015
  AngleOverride = false
  Arbitrary = false
  ArbitraryTolerances = false
  EqualTolerance = true
  ExtensionAngle = 0
  FormatSpec = %.2w
  FormatSpecOverTolerance = %+.2w
  FormatSpecUnderTolerance = %+.2w
  Inverted = false
  LineAngle = 0
  LockPosition = false
  MeasureType = 1
  OverTolerance = 0
  References2D = -> [View]
  Rotation = 0
  Scale = 0.75
  ScaleType = 0
  TheoreticalExact = false
  Type = 2
  UnderTolerance = 0
  X = -33.9407
  Y = 9.4798
FEATURE [TechDraw::DrawViewDimension] Dimension016
  AngleOverride = false
  Arbitrary = false
  ArbitraryTolerances = false
  EqualTolerance = true
  ExtensionAngle = 0
  FormatSpec = %.2w
  FormatSpecOverTolerance = %+.2w
  FormatSpecUnderTolerance = %+.2w
  Inverted = false
  LineAngle = 0
  LockPosition = false
  MeasureType = 1
  OverTolerance = 0
  References2D = -> [View]
  Rotation = 0
  Scale = 0.75
  ScaleType = 0
  TheoreticalExact = false
  Type = 1
  UnderTolerance = 0
  X = -15.7364
  Y = 20.6074
FEATURE [TechDraw::DrawViewDimension] Dimension017
  AngleOverride = false
  Arbitrary = false
  ArbitraryTolerances = false
  EqualTolerance = true
  ExtensionAngle = 0
  FormatSpec = %.2w
  FormatSpecOverTolerance = %+.2w
  FormatSpecUnderTolerance = %+.2w
  Inverted = false
  LineAngle = 0
  LockPosition = false
  MeasureType = 1
  OverTolerance = 0
  References2D = -> [View]
  Rotation = 0
  Scale = 0.75
  ScaleType = 0
  TheoreticalExact = false
  Type = 2
  UnderTolerance = 0
  X = 31.0381
  Y = -7.2272
FEATURE [TechDraw::DrawViewDimension] Dimension018
  AngleOverride = false
  Arbitrary = false
  ArbitraryTolerances = false
  EqualTolerance = true
  ExtensionAngle = 0
  FormatSpec = %.2w
  FormatSpecOverTolerance = %+.2w
  FormatSpecUnderTolerance = %+.2w
  Inverted = false
  LineAngle = 0
  LockPosition = false
  MeasureType = 1
  OverTolerance = 0
  References2D = -> [View]
  Rotation = 0
  Scale = 0.75
  ScaleType = 0
  TheoreticalExact = false
  Type = 2
  UnderTolerance = 0
  X = 39.7951
  Y = 5.90581
FEATURE [TechDraw::DrawViewDimension] Dimension019
  AngleOverride = false
  Arbitrary = false
  ArbitraryTolerances = false
  EqualTolerance = true
  ExtensionAngle = 0
  FormatSpec = %.2w
  FormatSpecOverTolerance = %+.2w
  FormatSpecUnderTolerance = %+.2w
  Inverted = false
  LineAngle = 0
  LockPosition = false
  MeasureType = 1
  OverTolerance = 0
  References2D = -> [View]
  Rotation = 0
  Scale = 0.75
  ScaleType = 0
  TheoreticalExact = false
  Type = 1
  UnderTolerance = 0
  X = -0.526118
  Y = 32.0801
FEATURE [TechDraw::DrawViewDimension] Dimension020
  AngleOverride = false
  Arbitrary = false
  ArbitraryTolerances = false
  EqualTolerance = true
  ExtensionAngle = 0
  FormatSpec = %.2w
  FormatSpecOverTolerance = %+.2w
  FormatSpecUnderTolerance = %+.2w
  Inverted = false
  LineAngle = 0
  LockPosition = false
  MeasureType = 1
  OverTolerance = 0
  References2D = -> [View]
  Rotation = 0
  Scale = 0.75
  ScaleType = 0
  TheoreticalExact = false
  Type = 1
  UnderTolerance = 0
  X = -32.8197
  Y = -5.56639
FEATURE [TechDraw::DrawViewPart] View004  label="Base Bottom"
  CoarseView = false
  Direction = (0,0,-1)
  Focus = 100
  HardHidden = false
  IsoCount = 0
  IsoHidden = false
  IsoVisible = false
  LockPosition = false
  Perspective = false
  Rotation = 0
  Scale = 0.75
  ScaleType = 0
  ScrubCount = 0
  SeamHidden = false
  SeamVisible = false
  SmoothHidden = false
  SmoothVisible = true
  Source = -> [Body001]
  X = 257.168
  XDirection = (0,-1,0)
  Y = 117.014
FEATURE [TechDraw::DrawViewPart] View005  label="Base Top"
  CoarseView = false
  Direction = (0,0,1)
  Focus = 100
  HardHidden = false
  IsoCount = 0
  IsoHidden = false
  IsoVisible = false
  LockPosition = false
  Perspective = false
  Rotation = 0
  Scale = 0.75
  ScaleType = 0
  ScrubCount = 0
  SeamHidden = false
  SeamVisible = false
  SmoothHidden = false
  SmoothVisible = true
  Source = -> [Body001]
  X = 169.73
  XDirection = (1,1e-06,0)
  Y = 90.8447
FEATURE [TechDraw::DrawViewDimension] Dimension021
  AngleOverride = false
  Arbitrary = false
  ArbitraryTolerances = false
  EqualTolerance = true
  ExtensionAngle = 0
  FormatSpec = %.2w
  FormatSpecOverTolerance = %+.2w
  FormatSpecUnderTolerance = %+.2w
  Inverted = false
  LineAngle = 0
  LockPosition = false
  MeasureType = 1
  OverTolerance = 0
  References2D = -> [View005]
  Rotation = 0
  Scale = 0.75
  ScaleType = 0
  TheoreticalExact = false
  Type = 1
  UnderTolerance = 0
  X = -1.79367
  Y = -11.5376
FEATURE [TechDraw::DrawViewDimension] Dimension022
  AngleOverride = false
  Arbitrary = false
  ArbitraryTolerances = false
  EqualTolerance = true
  ExtensionAngle = 0
  FormatSpec = %.2w
  FormatSpecOverTolerance = %+.2w
  FormatSpecUnderTolerance = %+.2w
  Inverted = false
  LineAngle = 0
  LockPosition = false
  MeasureType = 1
  OverTolerance = 0
  References2D = -> [View005]
  Rotation = 0
  Scale = 0.75
  ScaleType = 0
  TheoreticalExact = false
  Type = 2
  UnderTolerance = 0
  X = 52.3845
  Y = -9.54664
FEATURE [TechDraw::DrawViewDimension] Dimension023
  AngleOverride = false
  Arbitrary = false
  ArbitraryTolerances = false
  EqualTolerance = true
  ExtensionAngle = 0
  FormatSpec = %.2w
  FormatSpecOverTolerance = %+.2w
  FormatSpecUnderTolerance = %+.2w
  Inverted = false
  LineAngle = 0
  LockPosition = false
  MeasureType = 1
  OverTolerance = 0
  References2D = -> [View005]
  Rotation = 0
  Scale = 0.75
  ScaleType = 0
  TheoreticalExact = false
  Type = 2
  UnderTolerance = 0
  X = -58.4884
  Y = 3.29721
FEATURE [TechDraw::DrawViewDimension] Dimension024
  AngleOverride = false
  Arbitrary = false
  ArbitraryTolerances = false
  EqualTolerance = true
  ExtensionAngle = 0
  FormatSpec = %.2w
  FormatSpecOverTolerance = %+.2w
  FormatSpecUnderTolerance = %+.2w
  Inverted = false
  LineAngle = 0
  LockPosition = false
  MeasureType = 1
  OverTolerance = 0
  References2D = -> [View005]
  Rotation = 0
  Scale = 0.75
  ScaleType = 0
  TheoreticalExact = false
  Type = 1
  UnderTolerance = 0
  X = 0.075034
  Y = 30.9385
FEATURE [TechDraw::DrawViewDimension] Dimension025
  AngleOverride = false
  Arbitrary = false
  ArbitraryTolerances = false
  EqualTolerance = true
  ExtensionAngle = 0
  FormatSpec = %.2w
  FormatSpecOverTolerance = %+.2w
  FormatSpecUnderTolerance = %+.2w
  Inverted = false
  LineAngle = 0
  LockPosition = false
  MeasureType = 1
  OverTolerance = 0
  References2D = -> [View005]
  Rotation = 0
  Scale = 0.75
  ScaleType = 0
  TheoreticalExact = false
  Type = 1
  UnderTolerance = 0
  X = -1.03799
  Y = 40.381
FEATURE [TechDraw::DrawViewDimension] Dimension026
  AngleOverride = false
  Arbitrary = false
  ArbitraryTolerances = false
  EqualTolerance = true
  ExtensionAngle = 0
  FormatSpec = %.2w
  FormatSpecOverTolerance = %+.2w
  FormatSpecUnderTolerance = %+.2w
  Inverted = false
  LineAngle = 0
  LockPosition = false
  MeasureType = 1
  OverTolerance = 0
  References2D = -> [View005]
  Rotation = 0
  Scale = 0.75
  ScaleType = 0
  TheoreticalExact = false
  Type = 2
  UnderTolerance = 0
  X = -32.3206
  Y = 24.3456
FEATURE [TechDraw::DrawViewDimension] Dimension027
  AngleOverride = false
  Arbitrary = false
  ArbitraryTolerances = false
  EqualTolerance = true
  ExtensionAngle = 0
  FormatSpec = %.2w
  FormatSpecOverTolerance = %+.2w
  FormatSpecUnderTolerance = %+.2w
  Inverted = false
  LineAngle = 0
  LockPosition = false
  MeasureType = 1
  OverTolerance = 0
  References2D = -> [View005]
  Rotation = 0
  Scale = 0.75
  ScaleType = 0
  TheoreticalExact = false
  Type = 2
  UnderTolerance = 0
  X = -40.3549
  Y = 19.0344
FEATURE [TechDraw::DrawViewDimension] Dimension028
  AngleOverride = false
  Arbitrary = false
  ArbitraryTolerances = false
  EqualTolerance = true
  ExtensionAngle = 0
  FormatSpec = %.2w
  FormatSpecOverTolerance = %+.2w
  FormatSpecUnderTolerance = %+.2w
  Inverted = false
  LineAngle = 0
  LockPosition = false
  MeasureType = 1
  OverTolerance = 0
  References2D = -> [View005]
  Rotation = 0
  Scale = 0.75
  ScaleType = 0
  TheoreticalExact = false
  Type = 1
  UnderTolerance = 0
  X = 4.8544
  Y = 0.716886
FEATURE [TechDraw::DrawViewDimension] Dimension029
  AngleOverride = false
  Arbitrary = false
  ArbitraryTolerances = false
  EqualTolerance = true
  ExtensionAngle = 0
  FormatSpec = %.2w
  FormatSpecOverTolerance = %+.2w
  FormatSpecUnderTolerance = %+.2w
  Inverted = false
  LineAngle = 0
  LockPosition = false
  MeasureType = 1
  OverTolerance = 0
  References2D = -> [View005]
  Rotation = 0
  Scale = 0.75
  ScaleType = 0
  TheoreticalExact = false
  Type = 2
  UnderTolerance = 0
  X = -20.0012
  Y = 17.7369
FEATURE [TechDraw::DrawViewDimension] Dimension031
  AngleOverride = false
  Arbitrary = false
  ArbitraryTolerances = false
  EqualTolerance = true
  ExtensionAngle = 0
  FormatSpec = %.2w
  FormatSpecOverTolerance = %+.2w
  FormatSpecUnderTolerance = %+.2w
  Inverted = false
  LineAngle = 0
  LockPosition = false
  MeasureType = 1
  OverTolerance = 0
  References2D = -> [View005]
  Rotation = 0
  Scale = 0.75
  ScaleType = 0
  TheoreticalExact = false
  Type = 2
  UnderTolerance = 0
  X = 36.3885
  Y = 23.6837
FEATURE [TechDraw::DrawViewDimension] Dimension032
  AngleOverride = false
  Arbitrary = false
  ArbitraryTolerances = false
  EqualTolerance = true
  ExtensionAngle = 0
  FormatSpec = R%.2w
  FormatSpecOverTolerance = %+.2w
  FormatSpecUnderTolerance = %+.2w
  Inverted = false
  LineAngle = 0
  LockPosition = false
  MeasureType = 1
  OverTolerance = 0
  References2D = -> [View005]
  Rotation = 0
  Scale = 0.75
  ScaleType = 0
  TheoreticalExact = false
  Type = 4
  UnderTolerance = 0
  X = 53.4618
  Y = 6.68272
FEATURE [TechDraw::DrawViewDimension] Dimension033
  AngleOverride = false
  Arbitrary = false
  ArbitraryTolerances = false
  EqualTolerance = true
  ExtensionAngle = 0
  FormatSpec = ⌀%.2w
  FormatSpecOverTolerance = %+.2w
  FormatSpecUnderTolerance = %+.2w
  Inverted = false
  LineAngle = 0
  LockPosition = false
  MeasureType = 1
  OverTolerance = 0
  References2D = -> [View004]
  Rotation = 0
  Scale = 0.75
  ScaleType = 0
  TheoreticalExact = false
  Type = 5
  UnderTolerance = 0
  X = -7.6618
  Y = 52.4538
FEATURE [TechDraw::DrawViewDimension] Dimension034
  AngleOverride = false
  Arbitrary = false
  ArbitraryTolerances = false
  EqualTolerance = true
  ExtensionAngle = 0
  FormatSpec = %.2w
  FormatSpecOverTolerance = %+.2w
  FormatSpecUnderTolerance = %+.2w
  Inverted = false
  LineAngle = 0
  LockPosition = false
  MeasureType = 1
  OverTolerance = 0
  References2D = -> [View004]
  Rotation = 0
  Scale = 0.75
  ScaleType = 0
  TheoreticalExact = false
  Type = 1
  UnderTolerance = 0
  X = 1.83769
  Y = 69.3573
FEATURE [TechDraw::DrawViewDimension] Dimension035
  AngleOverride = false
  Arbitrary = false
  ArbitraryTolerances = false
  EqualTolerance = true
  ExtensionAngle = 0
  FormatSpec = %.2w
  FormatSpecOverTolerance = %+.2w
  FormatSpecUnderTolerance = %+.2w
  Inverted = false
  LineAngle = 0
  LockPosition = false
  MeasureType = 1
  OverTolerance = 0
  References2D = -> [View004]
  Rotation = 0
  Scale = 0.75
  ScaleType = 0
  TheoreticalExact = false
  Type = 1
  UnderTolerance = 0
  X = -30.7057
  Y = 34.8639
FEATURE [TechDraw::DrawViewDimension] Dimension036
  AngleOverride = false
  Arbitrary = false
  ArbitraryTolerances = false
  EqualTolerance = true
  ExtensionAngle = 0
  FormatSpec = %.2w
  FormatSpecOverTolerance = %+.2w
  FormatSpecUnderTolerance = %+.2w
  Inverted = false
  LineAngle = 0
  LockPosition = false
  MeasureType = 1
  OverTolerance = 0
  References2D = -> [View004]
  Rotation = 0
  Scale = 0.75
  ScaleType = 0
  TheoreticalExact = false
  Type = 1
  UnderTolerance = 0
  X = 2.10982
  Y = 61.9713
FEATURE [TechDraw::DrawViewDimension] Dimension038
  AngleOverride = false
  Arbitrary = false
  ArbitraryTolerances = false
  EqualTolerance = true
  ExtensionAngle = 0
  FormatSpec = R%.2w
  FormatSpecOverTolerance = %+.2w
  FormatSpecUnderTolerance = %+.2w
  Inverted = false
  LineAngle = 0
  LockPosition = false
  MeasureType = 1
  OverTolerance = 0
  References2D = -> [View004]
  Rotation = 0
  Scale = 0.75
  ScaleType = 0
  TheoreticalExact = false
  Type = 4
  UnderTolerance = 0
  X = 8.54047
  Y = 34.3087
FEATURE [TechDraw::DrawViewDimension] Dimension039
  AngleOverride = false
  Arbitrary = false
  ArbitraryTolerances = false
  EqualTolerance = true
  ExtensionAngle = 0
  FormatSpec = ⌀%.2w
  FormatSpecOverTolerance = %+.2w
  FormatSpecUnderTolerance = %+.2w
  Inverted = false
  LineAngle = 0
  LockPosition = false
  MeasureType = 1
  OverTolerance = 0
  References2D = -> [View004]
  Rotation = 0
  Scale = 0.75
  ScaleType = 0
  TheoreticalExact = false
  Type = 5
  UnderTolerance = 0
  X = 7.87854
  Y = -38.9181
FEATURE [TechDraw::DrawViewDimension] Dimension040
  AngleOverride = false
  Arbitrary = false
  ArbitraryTolerances = false
  EqualTolerance = true
  ExtensionAngle = 0
  FormatSpec = %.2w
  FormatSpecOverTolerance = %+.2w
  FormatSpecUnderTolerance = %+.2w
  Inverted = false
  LineAngle = 0
  LockPosition = false
  MeasureType = 1
  OverTolerance = 0
  References2D = -> [View002]
  Rotation = 0
  Scale = 0.75
  ScaleType = 0
  TheoreticalExact = false
  Type = 2
  UnderTolerance = 0
  X = -3.37408
  Y = -34.5629
FEATURE [TechDraw::DrawPage] Page
  KeepUpdated = true
  NextBalloonIndex = 1
  ProjectionType = 0
  Scale = 0.75
  Template = -> Template
  Views = -> [View002,Dimension,Dimension001,Dimension002,Dimension003,Dimension004,Dimension005,Dimension006,Dimension008,Dimension009,Dimension010,Dimension011,Dimension012,Dimension013,Dimension014,View,Dimension015,Dimension016,Dimension017,Dimension018,Dimension019,Dimension020,View004,View005,Dimension021,Dimension022,Dimension023,Dimension024,Dimension025,Dimension026,Dimension027,Dimension028,+10 more]
